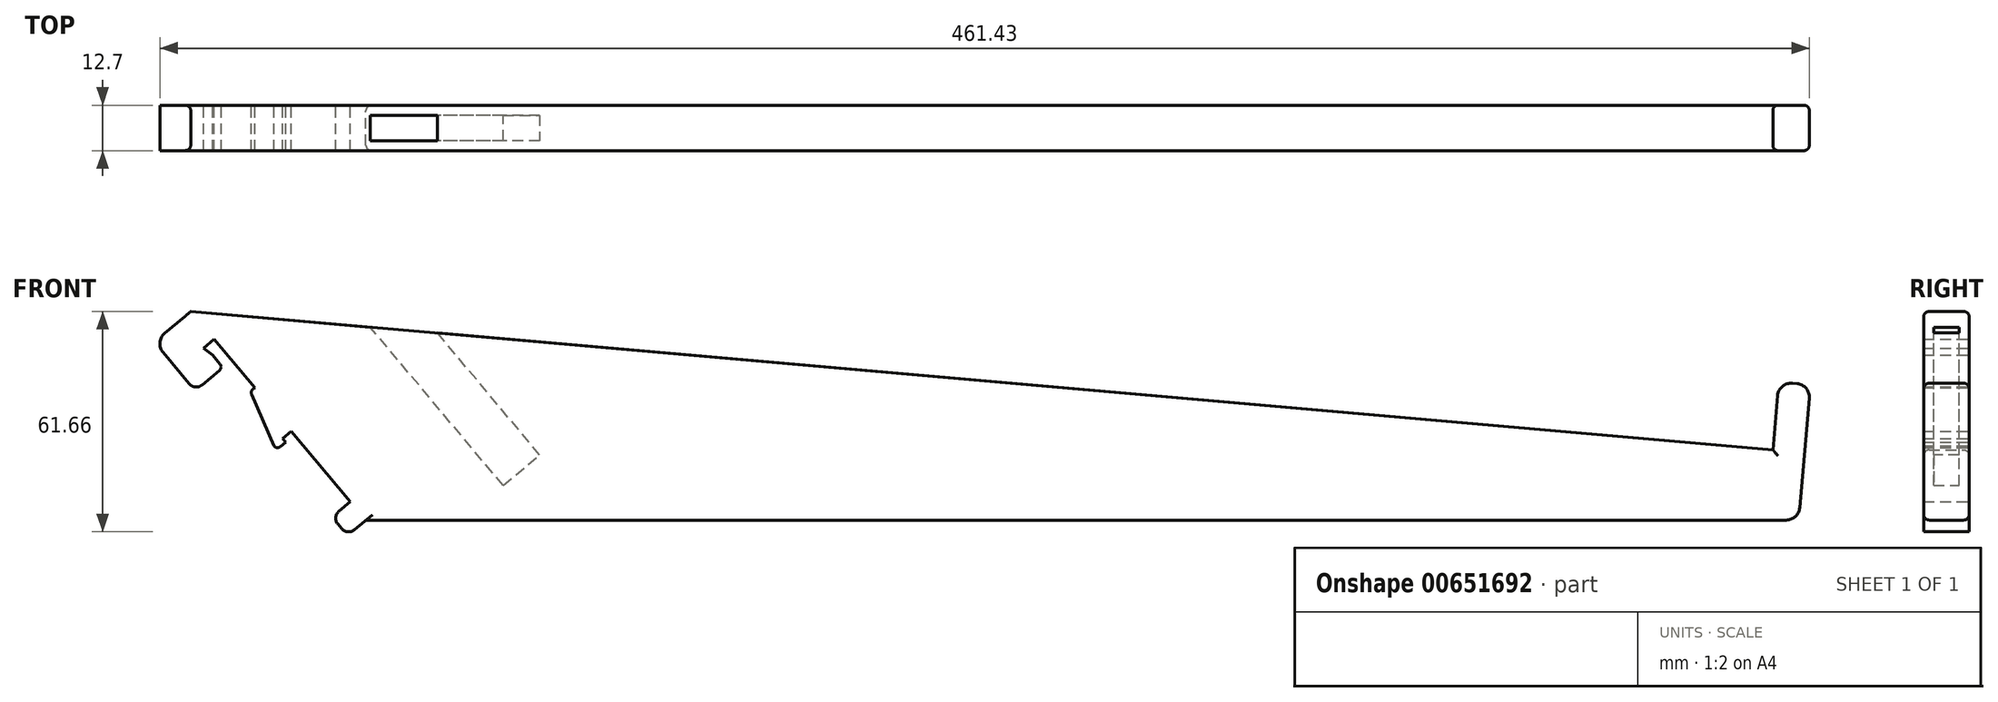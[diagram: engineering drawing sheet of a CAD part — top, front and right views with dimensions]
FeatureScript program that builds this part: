
annotation { "Feature Type Name" : "Feature", "Feature Type Description" : "" }
export const myFeature = defineFeature(function(context is Context, id is Id, definition is map)
    precondition{}
    {
        {
            var Q0;
            Q0=qCreatedBy(makeId("Front.planeOp"),FACE);
            var sketch = newSketch(context, id + "F0", { "sketchPlane" : qUnion([Q0])});
            skLineSegment(sketch, "E0.left", {"start": v(-46.53, -20.75) * mm, "end": v(-39.18, -29.5) * mm});
            skLineSegment(sketch, "E1", {"start": v(-38.77, -9.26) * mm, "end": v(403.81, -47.98) * mm});
            skLineSegment(sketch, "E2", {"start": v(403.81, -47.98) * mm, "end": v(405.14, -32.8) * mm});
            skLineSegment(sketch, "E3", {"start": v(10.22, -67.63) * mm, "end": v(407.53, -67.63) * mm});
            skPoint(sketch, "E4.start.orphan", {"position": v(-14.28, -38.44) * mm});
            skLineSegment(sketch, "E5.0", {"start": v(411.32, -64.15) * mm, "end": v(414, -33.57) * mm});
            skLineSegment(sketch, "E6.0", {"start": v(409.27, -29.33) * mm, "end": v(410.53, -29.44) * mm});
            skLineSegment(sketch, "E7", {"start": v(-46.06, -15.38) * mm, "end": v(-38.77, -9.26) * mm});
            skLineSegment(sketch, "E8", {"start": v(7, -70.32) * mm, "end": v(10.22, -67.63) * mm});
            skLineSegment(sketch, "E9.0", {"start": v(-12.22, -45.83) * mm, "end": v(-13.03, -44.86) * mm});
            skLineSegment(sketch, "E10.0", {"start": v(-35.6, -29.82) * mm, "end": v(-30.74, -25.73) * mm});
            skLineSegment(sketch, "E11.0", {"start": v(-30.58, -23.94) * mm, "end": v(-32.63, -21.51) * mm});
            skLineSegment(sketch, "E12.0", {"start": v(5.89, -62.47) * mm, "end": v(-10.6, -42.82) * mm});
            skLineSegment(sketch, "E13", {"start": v(-39.18, -29.5) * mm, "end": v(-46.53, -20.75) * mm});
            skLineSegment(sketch, "E14", {"start": v(-35.22, -19.55) * mm, "end": v(-32.23, -17.04) * mm});
            skPoint(sketch, "E15.newPointA", {"position": v(0, -76.2) * mm});
            skArc(sketch, "E15.filletArc", {"start": v(-39.18, -29.5) * mm, "mid": v(-37.46, -30.4) * mm, "end": v(-35.6, -29.82) * mm});
            skArc(sketch, "E16.filletArc", {"start": v(-30.74, -25.73) * mm, "mid": v(-30.3, -24.87) * mm, "end": v(-30.58, -23.94) * mm});
            skLineSegment(sketch, "E17.0", {"start": v(-13.03, -44.86) * mm, "end": v(-10.6, -42.82) * mm});
            skLineSegment(sketch, "E18.0", {"start": v(6.99, -43.82) * mm, "end": v(6.99, -43.82) * mm});
            skLineSegment(sketch, "E19.0", {"start": v(-13.68, -47.06) * mm, "end": v(-12.22, -45.83) * mm});
            skLineSegment(sketch, "E20.0", {"start": v(-21.37, -30.97) * mm, "end": v(-20.89, -30.56) * mm});
            skLineSegment(sketch, "E21", {"start": v(-21.72, -32.45) * mm, "end": v(-15.47, -46.9) * mm});
            skLineSegment(sketch, "E22.trimOffspring", {"start": v(-20.89, -30.56) * mm, "end": v(-32.23, -17.04) * mm});
            skLineSegment(sketch, "E23.0", {"start": v(2.68, -65.17) * mm, "end": v(5.89, -62.47) * mm});
            skLineSegment(sketch, "E24.0", {"start": v(3.43, -70) * mm, "end": v(2.37, -68.74) * mm});
            skPoint(sketch, "E25.visualSharp", {"position": v(0.73, -66.8) * mm});
            skArc(sketch, "E25.filletArc", {"start": v(2.68, -65.17) * mm, "mid": v(1.78, -66.9) * mm, "end": v(2.37, -68.74) * mm});
            skPoint(sketch, "E26.visualSharp", {"position": v(5.06, -71.96) * mm});
            skArc(sketch, "E26.filletArc", {"start": v(3.43, -70) * mm, "mid": v(5.15, -70.9) * mm, "end": v(7, -70.32) * mm});
            skPoint(sketch, "E27.visualSharp", {"position": v(-14.65, -47.87) * mm});
            skArc(sketch, "E27.filletArc", {"start": v(-15.47, -46.9) * mm, "mid": v(-14.6, -47.35) * mm, "end": v(-13.68, -47.06) * mm});
            skPoint(sketch, "E28.visualSharp", {"position": v(-22.1, -31.58) * mm});
            skArc(sketch, "E28.filletArc", {"start": v(-21.37, -30.97) * mm, "mid": v(-21.8, -31.65) * mm, "end": v(-21.72, -32.45) * mm});
            skArc(sketch, "E29.filletArc", {"start": v(407.53, -67.63) * mm, "mid": v(410.1, -66.63) * mm, "end": v(411.32, -64.15) * mm});
            skPoint(sketch, "E30.visualSharp", {"position": v(414.33, -29.77) * mm});
            skArc(sketch, "E30.filletArc", {"start": v(414, -33.57) * mm, "mid": v(413.12, -30.79) * mm, "end": v(410.53, -29.44) * mm});
            skPoint(sketch, "E31.visualSharp", {"position": v(405.47, -29) * mm});
            skArc(sketch, "E31.filletArc", {"start": v(409.27, -29.33) * mm, "mid": v(406.49, -30.2) * mm, "end": v(405.14, -32.8) * mm});
            skPoint(sketch, "E32.visualSharp", {"position": v(-48.98, -17.83) * mm});
            skArc(sketch, "E32.filletArc", {"start": v(-46.06, -15.38) * mm, "mid": v(-47.4, -17.96) * mm, "end": v(-46.53, -20.75) * mm});
            skLineSegment(sketch, "E33", {"start": v(-32.63, -21.51) * mm, "end": v(-35.22, -19.55) * mm});
            skPoint(sketch, "E34.orphan", {"position": v(-34.67, -19.08) * mm});
            skSolve(sketch);
        }
        {
            var Q0;
            Q0 = qSketchRegion(id + "F0", true);
            extrude(context, id + "F1", {"entities" : qUnion([Q0]), "depth" : 12.7 * mm, "offsetDistance" : 25.4 * mm});
        }
        {
            var Q0;
            Q0=makeQuery(id+"F1.opExtrude","SWEPT_FACE",FACE,{"disambiguationData":[OSD([sQuery(id+"F0.wireOp",EDGE,"E7")])]});
            var sketch = newSketch(context, id + "F2", { "sketchPlane" : qUnion([Q0])});
            skLineSegment(sketch, "E35.0", {"start": v(0, -2.8) * mm, "end": v(13.34, -2.8) * mm});
            skLineSegment(sketch, "E36.0", {"start": v(13.34, -9.9) * mm, "end": v(0, -9.9) * mm});
            skLineSegment(sketch, "E37", {"start": v(13.34, -2.8) * mm, "end": v(13.34, -9.9) * mm});
            skLineSegment(sketch, "E38", {"start": v(0, -9.9) * mm, "end": v(0, -2.8) * mm});
            skSolve(sketch);
        }
        {
            var Q0;
            Q0 = qSketchRegion(id + "F2", true);
            extrude(context, id + "F3", {"entities" : qUnion([Q0]), "operationType" : NewBodyOperationType.REMOVE, "oppositeDirection" : true, "depth" : 93.47 * mm, "offsetDistance" : 25.4 * mm});
        }
        {
            var Q0;
            Q0=makeQuery(id+"F1.opExtrude","CAP_FACE",FACE,{"disambiguationData":[OSD([sQuery(id+"F0.wireOp",EDGE,"E1"),sQuery(id+"F0.wireOp",EDGE,"E2"),sQuery(id+"F0.wireOp",EDGE,"E3"),sQuery(id+"F0.wireOp",EDGE,"E5.0"),sQuery(id+"F0.wireOp",EDGE,"E6.0"),sQuery(id+"F0.wireOp",EDGE,"E7"),sQuery(id+"F0.wireOp",EDGE,"E8"),sQuery(id+"F0.wireOp",EDGE,"E9.0"),sQuery(id+"F0.wireOp",EDGE,"E10.0"),sQuery(id+"F0.wireOp",EDGE,"E12.0"),sQuery(id+"F0.wireOp",EDGE,"E13"),sQuery(id+"F0.wireOp",EDGE,"E14"),sQuery(id+"F0.wireOp",EDGE,"E15.filletArc"),sQuery(id+"F0.wireOp",EDGE,"E16.filletArc"),sQuery(id+"F0.wireOp",EDGE,"E17.0"),sQuery(id+"F0.wireOp",EDGE,"E19.0"),sQuery(id+"F0.wireOp",EDGE,"E20.0"),sQuery(id+"F0.wireOp",EDGE,"E11.0"),sQuery(id+"F0.wireOp",EDGE,"E21"),sQuery(id+"F0.wireOp",EDGE,"E22.trimOffspring"),sQuery(id+"F0.wireOp",EDGE,"E23.0"),sQuery(id+"F0.wireOp",EDGE,"E24.0"),sQuery(id+"F0.wireOp",EDGE,"E25.filletArc"),sQuery(id+"F0.wireOp",EDGE,"E26.filletArc"),sQuery(id+"F0.wireOp",EDGE,"E27.filletArc"),sQuery(id+"F0.wireOp",EDGE,"E28.filletArc"),sQuery(id+"F0.wireOp",EDGE,"E29.filletArc"),sQuery(id+"F0.wireOp",EDGE,"E30.filletArc"),sQuery(id+"F0.wireOp",EDGE,"E31.filletArc")])],"isStart":false});
            var sketch = newSketch(context, id + "F4", { "sketchPlane" : qUnion([Q0])});
            skLineSegment(sketch, "E39.0", {"start": v(83.44, -160.14) * mm, "end": v(110.76, -132.83) * mm});
            skLineSegment(sketch, "E40.0", {"start": v(101.78, -132.83) * mm, "end": v(106.27, -128.34) * mm});
            skLineSegment(sketch, "E41.0", {"start": v(106.27, -128.34) * mm, "end": v(110.76, -132.83) * mm});
            skLineSegment(sketch, "E42.0", {"start": v(115.25, -119.36) * mm, "end": v(119.74, -123.85) * mm});
            skLineSegment(sketch, "E43.0", {"start": v(97.29, -128.34) * mm, "end": v(115.25, -110.38) * mm});
            skLineSegment(sketch, "E44.0", {"start": v(97.29, -128.34) * mm, "end": v(101.78, -132.83) * mm});
            skLineSegment(sketch, "E45.0", {"start": v(115.25, -110.38) * mm, "end": v(119.74, -114.87) * mm});
            skLineSegment(sketch, "E46.trimOffspring", {"start": v(115.25, -119.36) * mm, "end": v(119.74, -114.87) * mm});
            skLineSegment(sketch, "E47.trimOffspring", {"start": v(119.74, -123.85) * mm, "end": v(147.06, -96.53) * mm});
            skLineSegment(sketch, "E48.0", {"start": v(83.32, -160.02) * mm, "end": v(110.5, -132.83) * mm});
            skLineSegment(sketch, "E49.0", {"start": v(106.27, -128.59) * mm, "end": v(110.5, -132.83) * mm});
            skLineSegment(sketch, "E50.0", {"start": v(101.78, -133.08) * mm, "end": v(106.27, -128.59) * mm});
            skLineSegment(sketch, "E51.0", {"start": v(97.04, -128.34) * mm, "end": v(101.78, -133.08) * mm});
            skLineSegment(sketch, "E52.0", {"start": v(97.04, -128.34) * mm, "end": v(115.25, -110.12) * mm});
            skLineSegment(sketch, "E53.0", {"start": v(115.25, -110.12) * mm, "end": v(120, -114.87) * mm});
            skLineSegment(sketch, "E54.0", {"start": v(115.5, -119.36) * mm, "end": v(120, -114.87) * mm});
            skLineSegment(sketch, "E55.0", {"start": v(115.5, -119.36) * mm, "end": v(119.74, -123.6) * mm});
            skLineSegment(sketch, "E56.0", {"start": v(119.74, -123.6) * mm, "end": v(146.93, -96.4) * mm});
            skLineSegment(sketch, "E57", {"start": v(83.44, -160.14) * mm, "end": v(83.32, -160.02) * mm});
            skLineSegment(sketch, "E58", {"start": v(147.06, -96.53) * mm, "end": v(146.93, -96.4) * mm});
            skLineSegment(sketch, "E59", {"start": v(249.56, -199.03) * mm, "end": v(224.81, -223.77) * mm});
            skLineSegment(sketch, "E60", {"start": v(222.59, -217.02) * mm, "end": v(220.32, -219.28) * mm});
            skLineSegment(sketch, "E61.0", {"start": v(218.1, -212.53) * mm, "end": v(203.82, -226.8) * mm});
            skLineSegment(sketch, "E62.0", {"start": v(220.32, -219.28) * mm, "end": v(224.81, -223.77) * mm});
            skLineSegment(sketch, "E63.0", {"start": v(210.57, -229.03) * mm, "end": v(215.06, -233.52) * mm});
            skLineSegment(sketch, "E64.0", {"start": v(218.1, -212.53) * mm, "end": v(222.59, -217.02) * mm});
            skLineSegment(sketch, "E65.0", {"start": v(203.82, -226.8) * mm, "end": v(208.3, -231.3) * mm});
            skLineSegment(sketch, "E66.trimOffspring", {"start": v(210.57, -229.03) * mm, "end": v(208.3, -231.3) * mm});
            skLineSegment(sketch, "E67.trimOffspring", {"start": v(215.06, -233.52) * mm, "end": v(190.29, -258.3) * mm});
            skLineSegment(sketch, "E68.0", {"start": v(249.43, -198.9) * mm, "end": v(224.81, -223.52) * mm});
            skLineSegment(sketch, "E68.1", {"start": v(220.58, -219.28) * mm, "end": v(224.81, -223.52) * mm});
            skLineSegment(sketch, "E68.2", {"start": v(222.84, -217.02) * mm, "end": v(220.58, -219.28) * mm});
            skLineSegment(sketch, "E68.3", {"start": v(218.1, -212.28) * mm, "end": v(222.84, -217.02) * mm});
            skLineSegment(sketch, "E68.4", {"start": v(218.1, -212.28) * mm, "end": v(203.57, -226.8) * mm});
            skLineSegment(sketch, "E68.5", {"start": v(214.8, -233.52) * mm, "end": v(190.16, -258.17) * mm});
            skLineSegment(sketch, "E68.6", {"start": v(210.57, -229.29) * mm, "end": v(214.8, -233.52) * mm});
            skLineSegment(sketch, "E68.7", {"start": v(210.57, -229.29) * mm, "end": v(208.3, -231.55) * mm});
            skLineSegment(sketch, "E68.8", {"start": v(203.57, -226.8) * mm, "end": v(208.3, -231.55) * mm});
            skLineSegment(sketch, "E69", {"start": v(190.29, -258.3) * mm, "end": v(190.16, -258.17) * mm});
            skLineSegment(sketch, "E70", {"start": v(249.56, -199.03) * mm, "end": v(249.43, -198.9) * mm});
            skSolve(sketch);
        }
        {
            var Q0;
            {var subQ0=sQuery(id+"F0.wireOp",EDGE,"E1");var subQ1=sQuery(id+"F0.wireOp",EDGE,"E7");Q0=makeQuery(id+"FWbcaWF1RjLIeFM_1.boolean.opBoolean","SPLIT",EDGE,{"disambiguationData":[TD([makeQuery(id+"F1.opExtrude","SWEPT_FACE",FACE,{"disambiguationData":[OSD([subQ1])]})])],"derivedFrom":makeQuery(id+"F1.opExtrude","CAP_EDGE",EDGE,{"disambiguationData":[OSD([subQ0])],"isStart":true})});}
            var Q1;
            {var subQ0=sQuery(id+"F0.wireOp",EDGE,"E1");Q1=makeQuery(id+"FWbcaWF1RjLIeFM_1.boolean.opBoolean","SPLIT",EDGE,{"disambiguationData":[TD([makeQuery(id+"FWbcaWF1RjLIeFM_1.opExtrude","SWEPT_FACE",FACE,{"disambiguationData":[OSD([sQuery(id+"F4.wireOp",EDGE,"E47.trimOffspring")])]})])],"derivedFrom":makeQuery(id+"F1.opExtrude","CAP_EDGE",EDGE,{"disambiguationData":[OSD([subQ0])],"isStart":true})});}
            var Q2;
            {var subQ0=sQuery(id+"F0.wireOp",EDGE,"E1");var subQ1=sQuery(id+"F0.wireOp",EDGE,"E2");Q2=makeQuery(id+"FWbcaWF1RjLIeFM_1.boolean.opBoolean","SPLIT",EDGE,{"disambiguationData":[TD([makeQuery(id+"F1.opExtrude","SWEPT_FACE",FACE,{"disambiguationData":[OSD([subQ1])]})])],"derivedFrom":makeQuery(id+"F1.opExtrude","CAP_EDGE",EDGE,{"disambiguationData":[OSD([subQ0])],"isStart":true})});}
            var Q3;
            Q3=makeQuery(id+"F1.opExtrude","CAP_EDGE",EDGE,{"disambiguationData":[OSD([sQuery(id+"F0.wireOp",EDGE,"E2")])],"isStart":true});
            var Q4;
            {var subQ0=sQuery(id+"F0.wireOp",EDGE,"E3");Q4=makeQuery(id+"FWbcaWF1RjLIeFM_1.boolean.opBoolean","SPLIT",EDGE,{"disambiguationData":[TD([makeQuery(id+"FWbcaWF1RjLIeFM_1.opExtrude","SWEPT_FACE",FACE,{"disambiguationData":[OSD([sQuery(id+"F4.wireOp",EDGE,"E39.0")])]})])],"derivedFrom":makeQuery(id+"F1.opExtrude","CAP_EDGE",EDGE,{"disambiguationData":[OSD([subQ0])],"isStart":true})});}
            var Q5;
            {var subQ0=sQuery(id+"F0.wireOp",EDGE,"E8");var subQ1=sQuery(id+"F0.wireOp",EDGE,"E3");Q5=makeQuery(id+"FWbcaWF1RjLIeFM_1.boolean.opBoolean","SPLIT",EDGE,{"disambiguationData":[TD([makeQuery(id+"F1.opExtrude","SWEPT_FACE",FACE,{"disambiguationData":[OSD([subQ0])]})])],"derivedFrom":makeQuery(id+"F1.opExtrude","CAP_EDGE",EDGE,{"disambiguationData":[OSD([subQ1])],"isStart":true})});}
            fillet(context, id + "F5", {"entities" : qUnion([Q0, Q1, Q2, Q3, Q4, Q5]), "radius" : 1.52 * mm, "tangentPropagation" : true, "allowEdgeOverflow" : false});
        }
        {
            var Q0;
            {var subQ0=sQuery(id+"F0.wireOp",EDGE,"E1");var subQ1=sQuery(id+"F0.wireOp",EDGE,"E7");Q0=makeQuery(id+"FWbcaWF1RjLIeFM_1.boolean.opBoolean","SPLIT",EDGE,{"disambiguationData":[TD([makeQuery(id+"F1.opExtrude","SWEPT_FACE",FACE,{"disambiguationData":[OSD([subQ1])]})])],"derivedFrom":makeQuery(id+"F1.opExtrude","CAP_EDGE",EDGE,{"disambiguationData":[OSD([subQ0])],"isStart":false})});}
            var Q1;
            {var subQ0=sQuery(id+"F0.wireOp",EDGE,"E1");Q1=makeQuery(id+"FWbcaWF1RjLIeFM_1.boolean.opBoolean","SPLIT",EDGE,{"disambiguationData":[TD([makeQuery(id+"FWbcaWF1RjLIeFM_1.opExtrude","SWEPT_FACE",FACE,{"disambiguationData":[OSD([sQuery(id+"F4.wireOp",EDGE,"E47.trimOffspring")])]})])],"derivedFrom":makeQuery(id+"F1.opExtrude","CAP_EDGE",EDGE,{"disambiguationData":[OSD([subQ0])],"isStart":false})});}
            var Q2;
            {var subQ0=sQuery(id+"F0.wireOp",EDGE,"E1");var subQ1=sQuery(id+"F0.wireOp",EDGE,"E2");Q2=makeQuery(id+"FWbcaWF1RjLIeFM_1.boolean.opBoolean","SPLIT",EDGE,{"disambiguationData":[TD([makeQuery(id+"F1.opExtrude","SWEPT_FACE",FACE,{"disambiguationData":[OSD([subQ1])]})])],"derivedFrom":makeQuery(id+"F1.opExtrude","CAP_EDGE",EDGE,{"disambiguationData":[OSD([subQ0])],"isStart":false})});}
            var Q3;
            Q3=makeQuery(id+"F1.opExtrude","CAP_EDGE",EDGE,{"disambiguationData":[OSD([sQuery(id+"F0.wireOp",EDGE,"E2")])],"isStart":false});
            var Q4;
            {var subQ0=sQuery(id+"F0.wireOp",EDGE,"E3");Q4=makeQuery(id+"FWbcaWF1RjLIeFM_1.boolean.opBoolean","SPLIT",EDGE,{"disambiguationData":[TD([makeQuery(id+"FWbcaWF1RjLIeFM_1.opExtrude","SWEPT_FACE",FACE,{"disambiguationData":[OSD([sQuery(id+"F4.wireOp",EDGE,"E39.0")])]})])],"derivedFrom":makeQuery(id+"F1.opExtrude","CAP_EDGE",EDGE,{"disambiguationData":[OSD([subQ0])],"isStart":false})});}
            var Q5;
            {var subQ0=sQuery(id+"F0.wireOp",EDGE,"E8");var subQ1=sQuery(id+"F0.wireOp",EDGE,"E3");Q5=makeQuery(id+"FWbcaWF1RjLIeFM_1.boolean.opBoolean","SPLIT",EDGE,{"disambiguationData":[TD([makeQuery(id+"F1.opExtrude","SWEPT_FACE",FACE,{"disambiguationData":[OSD([subQ0])]})])],"derivedFrom":makeQuery(id+"F1.opExtrude","CAP_EDGE",EDGE,{"disambiguationData":[OSD([subQ1])],"isStart":false})});}
            fillet(context, id + "F6", {"entities" : qUnion([Q0, Q1, Q2, Q3, Q4, Q5]), "radius" : 1.52 * mm, "tangentPropagation" : true, "allowEdgeOverflow" : false});
        }
    });
